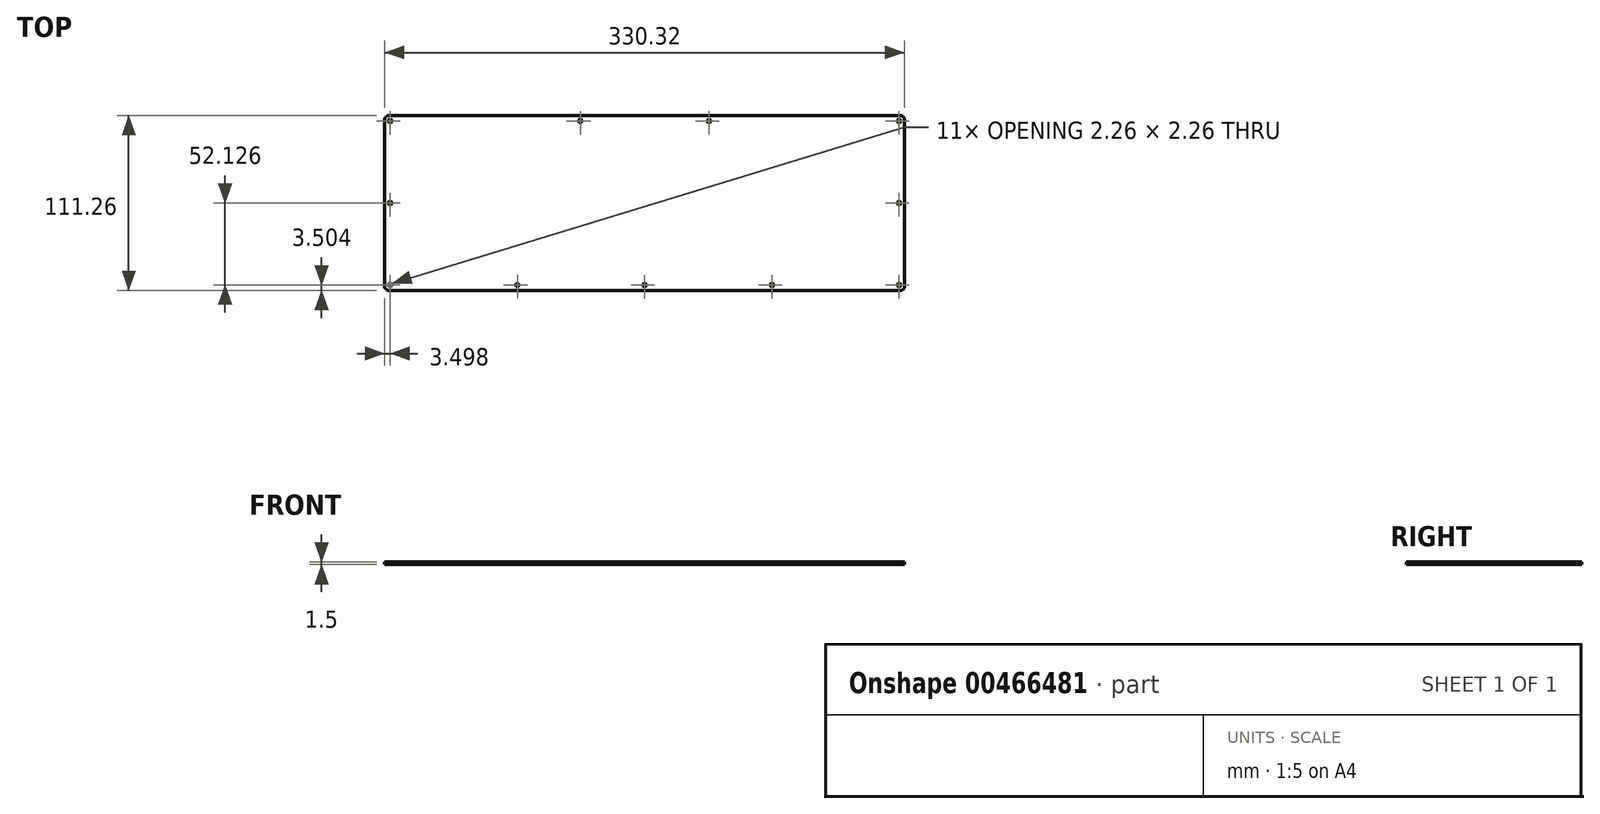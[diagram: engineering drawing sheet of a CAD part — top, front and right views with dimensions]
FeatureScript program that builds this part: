
annotation { "Feature Type Name" : "Feature", "Feature Type Description" : "" }
export const myFeature = defineFeature(function(context is Context, id is Id, definition is map)
    precondition{}
    {
        {
            var Q0;
            Q0=qCreatedBy(makeId("Top.planeOp"),FACE);
            var sketch = newSketch(context, id + "F0", { "sketchPlane" : qUnion([Q0])});
            skLineSegment(sketch, "E0", {"start": v(162.16, 55.62) * mm, "end": v(162.4, 55.62) * mm});
            skLineSegment(sketch, "E1", {"start": v(162.4, 55.62) * mm, "end": v(162.63, 55.59) * mm});
            skLineSegment(sketch, "E2", {"start": v(162.63, 55.59) * mm, "end": v(162.86, 55.54) * mm});
            skLineSegment(sketch, "E3", {"start": v(162.86, 55.54) * mm, "end": v(163.1, 55.48) * mm});
            skLineSegment(sketch, "E4", {"start": v(163.1, 55.48) * mm, "end": v(163.31, 55.4) * mm});
            skLineSegment(sketch, "E5", {"start": v(163.31, 55.4) * mm, "end": v(163.53, 55.3) * mm});
            skLineSegment(sketch, "E6", {"start": v(163.53, 55.3) * mm, "end": v(163.73, 55.18) * mm});
            skLineSegment(sketch, "E7", {"start": v(163.73, 55.18) * mm, "end": v(163.93, 55.05) * mm});
            skLineSegment(sketch, "E8", {"start": v(163.93, 55.05) * mm, "end": v(164.11, 54.9) * mm});
            skLineSegment(sketch, "E9", {"start": v(164.11, 54.9) * mm, "end": v(164.29, 54.75) * mm});
            skLineSegment(sketch, "E10", {"start": v(164.29, 54.75) * mm, "end": v(164.45, 54.57) * mm});
            skLineSegment(sketch, "E11", {"start": v(164.45, 54.57) * mm, "end": v(164.6, 54.39) * mm});
            skLineSegment(sketch, "E12", {"start": v(164.6, 54.39) * mm, "end": v(164.72, 54.2) * mm});
            skLineSegment(sketch, "E13", {"start": v(164.72, 54.2) * mm, "end": v(164.84, 53.99) * mm});
            skLineSegment(sketch, "E14", {"start": v(164.84, 53.99) * mm, "end": v(164.93, 53.77) * mm});
            skLineSegment(sketch, "E15", {"start": v(164.93, 53.77) * mm, "end": v(165.02, 53.55) * mm});
            skLineSegment(sketch, "E16", {"start": v(165.02, 53.55) * mm, "end": v(165.08, 53.33) * mm});
            skLineSegment(sketch, "E17", {"start": v(165.08, 53.33) * mm, "end": v(165.13, 53.1) * mm});
            skLineSegment(sketch, "E18", {"start": v(165.13, 53.1) * mm, "end": v(165.15, 52.86) * mm});
            skLineSegment(sketch, "E19", {"start": v(165.15, 52.86) * mm, "end": v(165.16, 52.62) * mm});
            skLineSegment(sketch, "E20", {"start": v(165.16, 52.62) * mm, "end": v(165.16, -52.63) * mm});
            skLineSegment(sketch, "E21", {"start": v(165.16, -52.63) * mm, "end": v(165.15, -52.86) * mm});
            skLineSegment(sketch, "E22", {"start": v(165.15, -52.86) * mm, "end": v(165.13, -53.1) * mm});
            skLineSegment(sketch, "E23", {"start": v(165.13, -53.1) * mm, "end": v(165.08, -53.33) * mm});
            skLineSegment(sketch, "E24", {"start": v(165.08, -53.33) * mm, "end": v(165.02, -53.55) * mm});
            skLineSegment(sketch, "E25", {"start": v(165.02, -53.55) * mm, "end": v(164.93, -53.77) * mm});
            skLineSegment(sketch, "E26", {"start": v(164.93, -53.77) * mm, "end": v(164.84, -53.99) * mm});
            skLineSegment(sketch, "E27", {"start": v(164.84, -53.99) * mm, "end": v(164.72, -54.2) * mm});
            skLineSegment(sketch, "E28", {"start": v(164.72, -54.2) * mm, "end": v(164.6, -54.39) * mm});
            skLineSegment(sketch, "E29", {"start": v(164.6, -54.39) * mm, "end": v(164.45, -54.57) * mm});
            skLineSegment(sketch, "E30", {"start": v(164.45, -54.57) * mm, "end": v(164.29, -54.75) * mm});
            skLineSegment(sketch, "E31", {"start": v(164.29, -54.75) * mm, "end": v(164.11, -54.9) * mm});
            skLineSegment(sketch, "E32", {"start": v(164.11, -54.9) * mm, "end": v(163.93, -55.05) * mm});
            skLineSegment(sketch, "E33", {"start": v(163.93, -55.05) * mm, "end": v(163.73, -55.18) * mm});
            skLineSegment(sketch, "E34", {"start": v(163.73, -55.18) * mm, "end": v(163.53, -55.3) * mm});
            skLineSegment(sketch, "E35", {"start": v(163.53, -55.3) * mm, "end": v(163.31, -55.4) * mm});
            skLineSegment(sketch, "E36", {"start": v(163.31, -55.4) * mm, "end": v(163.1, -55.48) * mm});
            skLineSegment(sketch, "E37", {"start": v(163.1, -55.48) * mm, "end": v(162.86, -55.54) * mm});
            skLineSegment(sketch, "E38", {"start": v(162.86, -55.54) * mm, "end": v(162.63, -55.59) * mm});
            skLineSegment(sketch, "E39", {"start": v(162.63, -55.59) * mm, "end": v(162.4, -55.62) * mm});
            skLineSegment(sketch, "E40", {"start": v(162.4, -55.62) * mm, "end": v(162.16, -55.63) * mm});
            skLineSegment(sketch, "E41", {"start": v(162.16, -55.63) * mm, "end": v(-162.16, -55.63) * mm});
            skLineSegment(sketch, "E42", {"start": v(-162.16, -55.63) * mm, "end": v(-162.4, -55.62) * mm});
            skLineSegment(sketch, "E43", {"start": v(-162.4, -55.62) * mm, "end": v(-162.63, -55.59) * mm});
            skLineSegment(sketch, "E44", {"start": v(-162.63, -55.59) * mm, "end": v(-162.86, -55.54) * mm});
            skLineSegment(sketch, "E45", {"start": v(-162.86, -55.54) * mm, "end": v(-163.09, -55.48) * mm});
            skLineSegment(sketch, "E46", {"start": v(-163.09, -55.48) * mm, "end": v(-163.31, -55.4) * mm});
            skLineSegment(sketch, "E47", {"start": v(-163.31, -55.4) * mm, "end": v(-163.52, -55.3) * mm});
            skLineSegment(sketch, "E48", {"start": v(-163.52, -55.3) * mm, "end": v(-163.73, -55.18) * mm});
            skLineSegment(sketch, "E49", {"start": v(-163.73, -55.18) * mm, "end": v(-163.93, -55.05) * mm});
            skLineSegment(sketch, "E50", {"start": v(-163.93, -55.05) * mm, "end": v(-164.11, -54.9) * mm});
            skLineSegment(sketch, "E51", {"start": v(-164.11, -54.9) * mm, "end": v(-164.28, -54.75) * mm});
            skLineSegment(sketch, "E52", {"start": v(-164.28, -54.75) * mm, "end": v(-164.44, -54.57) * mm});
            skLineSegment(sketch, "E53", {"start": v(-164.44, -54.57) * mm, "end": v(-164.6, -54.39) * mm});
            skLineSegment(sketch, "E54", {"start": v(-164.6, -54.39) * mm, "end": v(-164.72, -54.2) * mm});
            skLineSegment(sketch, "E55", {"start": v(-164.72, -54.2) * mm, "end": v(-164.84, -53.99) * mm});
            skLineSegment(sketch, "E56", {"start": v(-164.84, -53.99) * mm, "end": v(-164.93, -53.77) * mm});
            skLineSegment(sketch, "E57", {"start": v(-164.93, -53.77) * mm, "end": v(-165.02, -53.55) * mm});
            skLineSegment(sketch, "E58", {"start": v(-165.02, -53.55) * mm, "end": v(-165.08, -53.33) * mm});
            skLineSegment(sketch, "E59", {"start": v(-165.08, -53.33) * mm, "end": v(-165.13, -53.1) * mm});
            skLineSegment(sketch, "E60", {"start": v(-165.13, -53.1) * mm, "end": v(-165.15, -52.86) * mm});
            skLineSegment(sketch, "E61", {"start": v(-165.15, -52.86) * mm, "end": v(-165.16, -52.63) * mm});
            skLineSegment(sketch, "E62", {"start": v(-165.16, -52.63) * mm, "end": v(-165.16, 52.62) * mm});
            skLineSegment(sketch, "E63", {"start": v(-165.16, 52.62) * mm, "end": v(-165.15, 52.86) * mm});
            skLineSegment(sketch, "E64", {"start": v(-165.15, 52.86) * mm, "end": v(-165.13, 53.1) * mm});
            skLineSegment(sketch, "E65", {"start": v(-165.13, 53.1) * mm, "end": v(-165.08, 53.33) * mm});
            skLineSegment(sketch, "E66", {"start": v(-165.08, 53.33) * mm, "end": v(-165.02, 53.55) * mm});
            skLineSegment(sketch, "E67", {"start": v(-165.02, 53.55) * mm, "end": v(-164.93, 53.77) * mm});
            skLineSegment(sketch, "E68", {"start": v(-164.93, 53.77) * mm, "end": v(-164.84, 53.99) * mm});
            skLineSegment(sketch, "E69", {"start": v(-164.84, 53.99) * mm, "end": v(-164.72, 54.2) * mm});
            skLineSegment(sketch, "E70", {"start": v(-164.72, 54.2) * mm, "end": v(-164.6, 54.39) * mm});
            skLineSegment(sketch, "E71", {"start": v(-164.6, 54.39) * mm, "end": v(-164.44, 54.57) * mm});
            skLineSegment(sketch, "E72", {"start": v(-164.44, 54.57) * mm, "end": v(-164.28, 54.75) * mm});
            skLineSegment(sketch, "E73", {"start": v(-164.28, 54.75) * mm, "end": v(-164.11, 54.9) * mm});
            skLineSegment(sketch, "E74", {"start": v(-164.11, 54.9) * mm, "end": v(-163.93, 55.05) * mm});
            skLineSegment(sketch, "E75", {"start": v(-163.93, 55.05) * mm, "end": v(-163.73, 55.18) * mm});
            skLineSegment(sketch, "E76", {"start": v(-163.73, 55.18) * mm, "end": v(-163.52, 55.3) * mm});
            skLineSegment(sketch, "E77", {"start": v(-163.52, 55.3) * mm, "end": v(-163.31, 55.4) * mm});
            skLineSegment(sketch, "E78", {"start": v(-163.31, 55.4) * mm, "end": v(-163.09, 55.48) * mm});
            skLineSegment(sketch, "E79", {"start": v(-163.09, 55.48) * mm, "end": v(-162.86, 55.54) * mm});
            skLineSegment(sketch, "E80", {"start": v(-162.86, 55.54) * mm, "end": v(-162.63, 55.59) * mm});
            skLineSegment(sketch, "E81", {"start": v(-162.63, 55.59) * mm, "end": v(-162.4, 55.62) * mm});
            skLineSegment(sketch, "E82", {"start": v(-162.4, 55.62) * mm, "end": v(-162.16, 55.63) * mm});
            skLineSegment(sketch, "E83", {"start": v(-162.16, 55.63) * mm, "end": v(162.16, 55.62) * mm});
            skLineSegment(sketch, "E84", {"start": v(161.31, -51.05) * mm, "end": v(161, -51.21) * mm});
            skLineSegment(sketch, "E85", {"start": v(161, -51.21) * mm, "end": v(160.75, -51.46) * mm});
            skLineSegment(sketch, "E86", {"start": v(160.75, -51.46) * mm, "end": v(160.59, -51.78) * mm});
            skLineSegment(sketch, "E87", {"start": v(160.59, -51.78) * mm, "end": v(160.53, -52.13) * mm});
            skLineSegment(sketch, "E88", {"start": v(160.53, -52.13) * mm, "end": v(160.59, -52.48) * mm});
            skLineSegment(sketch, "E89", {"start": v(160.59, -52.48) * mm, "end": v(160.75, -52.79) * mm});
            skLineSegment(sketch, "E90", {"start": v(160.75, -52.79) * mm, "end": v(161, -53.04) * mm});
            skLineSegment(sketch, "E91", {"start": v(161, -53.04) * mm, "end": v(161.31, -53.2) * mm});
            skLineSegment(sketch, "E92", {"start": v(161.31, -53.2) * mm, "end": v(161.66, -53.26) * mm});
            skLineSegment(sketch, "E93", {"start": v(161.66, -53.26) * mm, "end": v(162.01, -53.2) * mm});
            skLineSegment(sketch, "E94", {"start": v(162.01, -53.2) * mm, "end": v(162.33, -53.04) * mm});
            skLineSegment(sketch, "E95", {"start": v(162.33, -53.04) * mm, "end": v(162.58, -52.79) * mm});
            skLineSegment(sketch, "E96", {"start": v(162.58, -52.79) * mm, "end": v(162.74, -52.48) * mm});
            skLineSegment(sketch, "E97", {"start": v(162.74, -52.48) * mm, "end": v(162.8, -52.13) * mm});
            skLineSegment(sketch, "E98", {"start": v(162.8, -52.13) * mm, "end": v(162.74, -51.78) * mm});
            skLineSegment(sketch, "E99", {"start": v(162.74, -51.78) * mm, "end": v(162.58, -51.46) * mm});
            skLineSegment(sketch, "E100", {"start": v(162.58, -51.46) * mm, "end": v(162.33, -51.21) * mm});
            skLineSegment(sketch, "E101", {"start": v(162.33, -51.21) * mm, "end": v(162.01, -51.05) * mm});
            skLineSegment(sketch, "E102", {"start": v(162.01, -51.05) * mm, "end": v(161.66, -51) * mm});
            skLineSegment(sketch, "E103", {"start": v(161.66, -51) * mm, "end": v(161.31, -51.05) * mm});
            skLineSegment(sketch, "E104", {"start": v(80.48, -51.05) * mm, "end": v(80.17, -51.21) * mm});
            skLineSegment(sketch, "E105", {"start": v(80.17, -51.21) * mm, "end": v(79.92, -51.46) * mm});
            skLineSegment(sketch, "E106", {"start": v(79.92, -51.46) * mm, "end": v(79.76, -51.78) * mm});
            skLineSegment(sketch, "E107", {"start": v(79.76, -51.78) * mm, "end": v(79.7, -52.13) * mm});
            skLineSegment(sketch, "E108", {"start": v(79.7, -52.13) * mm, "end": v(79.76, -52.48) * mm});
            skLineSegment(sketch, "E109", {"start": v(79.76, -52.48) * mm, "end": v(79.92, -52.79) * mm});
            skLineSegment(sketch, "E110", {"start": v(79.92, -52.79) * mm, "end": v(80.17, -53.04) * mm});
            skLineSegment(sketch, "E111", {"start": v(80.17, -53.04) * mm, "end": v(80.48, -53.2) * mm});
            skLineSegment(sketch, "E112", {"start": v(80.48, -53.2) * mm, "end": v(80.83, -53.26) * mm});
            skLineSegment(sketch, "E113", {"start": v(80.83, -53.26) * mm, "end": v(81.18, -53.2) * mm});
            skLineSegment(sketch, "E114", {"start": v(81.18, -53.2) * mm, "end": v(81.5, -53.04) * mm});
            skLineSegment(sketch, "E115", {"start": v(81.5, -53.04) * mm, "end": v(81.75, -52.79) * mm});
            skLineSegment(sketch, "E116", {"start": v(81.75, -52.79) * mm, "end": v(81.9, -52.48) * mm});
            skLineSegment(sketch, "E117", {"start": v(81.9, -52.48) * mm, "end": v(81.96, -52.13) * mm});
            skLineSegment(sketch, "E118", {"start": v(81.96, -52.13) * mm, "end": v(81.9, -51.78) * mm});
            skLineSegment(sketch, "E119", {"start": v(81.9, -51.78) * mm, "end": v(81.75, -51.46) * mm});
            skLineSegment(sketch, "E120", {"start": v(81.75, -51.46) * mm, "end": v(81.5, -51.21) * mm});
            skLineSegment(sketch, "E121", {"start": v(81.5, -51.21) * mm, "end": v(81.18, -51.05) * mm});
            skLineSegment(sketch, "E122", {"start": v(81.18, -51.05) * mm, "end": v(80.83, -51) * mm});
            skLineSegment(sketch, "E123", {"start": v(80.83, -51) * mm, "end": v(80.48, -51.05) * mm});
            skLineSegment(sketch, "E124", {"start": v(-0.35, -51.05) * mm, "end": v(-0.66, -51.21) * mm});
            skLineSegment(sketch, "E125", {"start": v(-0.66, -51.21) * mm, "end": v(-0.91, -51.46) * mm});
            skLineSegment(sketch, "E126", {"start": v(-0.91, -51.46) * mm, "end": v(-1.07, -51.78) * mm});
            skLineSegment(sketch, "E127", {"start": v(-1.07, -51.78) * mm, "end": v(-1.13, -52.13) * mm});
            skLineSegment(sketch, "E128", {"start": v(-1.13, -52.13) * mm, "end": v(-1.07, -52.48) * mm});
            skLineSegment(sketch, "E129", {"start": v(-1.07, -52.48) * mm, "end": v(-0.91, -52.79) * mm});
            skLineSegment(sketch, "E130", {"start": v(-0.91, -52.79) * mm, "end": v(-0.66, -53.04) * mm});
            skLineSegment(sketch, "E131", {"start": v(-0.66, -53.04) * mm, "end": v(-0.35, -53.2) * mm});
            skLineSegment(sketch, "E132", {"start": v(-0.35, -53.2) * mm, "end": v(0, -53.26) * mm});
            skLineSegment(sketch, "E133", {"start": v(0, -53.26) * mm, "end": v(0.35, -53.2) * mm});
            skLineSegment(sketch, "E134", {"start": v(0.35, -53.2) * mm, "end": v(0.67, -53.04) * mm});
            skLineSegment(sketch, "E135", {"start": v(0.67, -53.04) * mm, "end": v(0.92, -52.79) * mm});
            skLineSegment(sketch, "E136", {"start": v(0.92, -52.79) * mm, "end": v(1.07, -52.48) * mm});
            skLineSegment(sketch, "E137", {"start": v(1.07, -52.48) * mm, "end": v(1.13, -52.13) * mm});
            skLineSegment(sketch, "E138", {"start": v(1.13, -52.13) * mm, "end": v(1.07, -51.78) * mm});
            skLineSegment(sketch, "E139", {"start": v(1.07, -51.78) * mm, "end": v(0.92, -51.46) * mm});
            skLineSegment(sketch, "E140", {"start": v(0.92, -51.46) * mm, "end": v(0.67, -51.21) * mm});
            skLineSegment(sketch, "E141", {"start": v(0.67, -51.21) * mm, "end": v(0.35, -51.05) * mm});
            skLineSegment(sketch, "E142", {"start": v(0.35, -51.05) * mm, "end": v(0, -51) * mm});
            skLineSegment(sketch, "E143", {"start": v(0, -51) * mm, "end": v(-0.35, -51.05) * mm});
            skLineSegment(sketch, "E144", {"start": v(-81.18, -51.05) * mm, "end": v(-81.5, -51.21) * mm});
            skLineSegment(sketch, "E145", {"start": v(-81.5, -51.21) * mm, "end": v(-81.75, -51.46) * mm});
            skLineSegment(sketch, "E146", {"start": v(-81.75, -51.46) * mm, "end": v(-81.9, -51.78) * mm});
            skLineSegment(sketch, "E147", {"start": v(-81.9, -51.78) * mm, "end": v(-81.96, -52.13) * mm});
            skLineSegment(sketch, "E148", {"start": v(-81.96, -52.13) * mm, "end": v(-81.9, -52.48) * mm});
            skLineSegment(sketch, "E149", {"start": v(-81.9, -52.48) * mm, "end": v(-81.75, -52.79) * mm});
            skLineSegment(sketch, "E150", {"start": v(-81.75, -52.79) * mm, "end": v(-81.5, -53.04) * mm});
            skLineSegment(sketch, "E151", {"start": v(-81.5, -53.04) * mm, "end": v(-81.18, -53.2) * mm});
            skLineSegment(sketch, "E152", {"start": v(-81.18, -53.2) * mm, "end": v(-80.83, -53.26) * mm});
            skLineSegment(sketch, "E153", {"start": v(-80.83, -53.26) * mm, "end": v(-80.48, -53.2) * mm});
            skLineSegment(sketch, "E154", {"start": v(-80.48, -53.2) * mm, "end": v(-80.17, -53.04) * mm});
            skLineSegment(sketch, "E155", {"start": v(-80.17, -53.04) * mm, "end": v(-79.92, -52.79) * mm});
            skLineSegment(sketch, "E156", {"start": v(-79.92, -52.79) * mm, "end": v(-79.76, -52.48) * mm});
            skLineSegment(sketch, "E157", {"start": v(-79.76, -52.48) * mm, "end": v(-79.7, -52.13) * mm});
            skLineSegment(sketch, "E158", {"start": v(-79.7, -52.13) * mm, "end": v(-79.76, -51.78) * mm});
            skLineSegment(sketch, "E159", {"start": v(-79.76, -51.78) * mm, "end": v(-79.92, -51.46) * mm});
            skLineSegment(sketch, "E160", {"start": v(-79.92, -51.46) * mm, "end": v(-80.17, -51.21) * mm});
            skLineSegment(sketch, "E161", {"start": v(-80.17, -51.21) * mm, "end": v(-80.48, -51.05) * mm});
            skLineSegment(sketch, "E162", {"start": v(-80.48, -51.05) * mm, "end": v(-80.83, -51) * mm});
            skLineSegment(sketch, "E163", {"start": v(-80.83, -51) * mm, "end": v(-81.18, -51.05) * mm});
            skLineSegment(sketch, "E164", {"start": v(-162.01, -51.05) * mm, "end": v(-162.33, -51.21) * mm});
            skLineSegment(sketch, "E165", {"start": v(-162.33, -51.21) * mm, "end": v(-162.58, -51.46) * mm});
            skLineSegment(sketch, "E166", {"start": v(-162.58, -51.46) * mm, "end": v(-162.74, -51.78) * mm});
            skLineSegment(sketch, "E167", {"start": v(-162.74, -51.78) * mm, "end": v(-162.8, -52.13) * mm});
            skLineSegment(sketch, "E168", {"start": v(-162.8, -52.13) * mm, "end": v(-162.74, -52.48) * mm});
            skLineSegment(sketch, "E169", {"start": v(-162.74, -52.48) * mm, "end": v(-162.58, -52.79) * mm});
            skLineSegment(sketch, "E170", {"start": v(-162.58, -52.79) * mm, "end": v(-162.33, -53.04) * mm});
            skLineSegment(sketch, "E171", {"start": v(-162.33, -53.04) * mm, "end": v(-162.01, -53.2) * mm});
            skLineSegment(sketch, "E172", {"start": v(-162.01, -53.2) * mm, "end": v(-161.66, -53.26) * mm});
            skLineSegment(sketch, "E173", {"start": v(-161.66, -53.26) * mm, "end": v(-161.31, -53.2) * mm});
            skLineSegment(sketch, "E174", {"start": v(-161.31, -53.2) * mm, "end": v(-161, -53.04) * mm});
            skLineSegment(sketch, "E175", {"start": v(-161, -53.04) * mm, "end": v(-160.75, -52.79) * mm});
            skLineSegment(sketch, "E176", {"start": v(-160.75, -52.79) * mm, "end": v(-160.59, -52.48) * mm});
            skLineSegment(sketch, "E177", {"start": v(-160.59, -52.48) * mm, "end": v(-160.53, -52.13) * mm});
            skLineSegment(sketch, "E178", {"start": v(-160.53, -52.13) * mm, "end": v(-160.59, -51.78) * mm});
            skLineSegment(sketch, "E179", {"start": v(-160.59, -51.78) * mm, "end": v(-160.75, -51.46) * mm});
            skLineSegment(sketch, "E180", {"start": v(-160.75, -51.46) * mm, "end": v(-161, -51.21) * mm});
            skLineSegment(sketch, "E181", {"start": v(-161, -51.21) * mm, "end": v(-161.31, -51.05) * mm});
            skLineSegment(sketch, "E182", {"start": v(-161.31, -51.05) * mm, "end": v(-161.66, -51) * mm});
            skLineSegment(sketch, "E183", {"start": v(-161.66, -51) * mm, "end": v(-162.01, -51.05) * mm});
            skLineSegment(sketch, "E184", {"start": v(161.31, 1.08) * mm, "end": v(161, 0.91) * mm});
            skLineSegment(sketch, "E185", {"start": v(161, 0.91) * mm, "end": v(160.75, 0.66) * mm});
            skLineSegment(sketch, "E186", {"start": v(160.75, 0.66) * mm, "end": v(160.59, 0.35) * mm});
            skLineSegment(sketch, "E187", {"start": v(160.59, 0.35) * mm, "end": v(160.53, 0) * mm});
            skLineSegment(sketch, "E188", {"start": v(160.53, 0) * mm, "end": v(160.59, -0.35) * mm});
            skLineSegment(sketch, "E189", {"start": v(160.59, -0.35) * mm, "end": v(160.75, -0.66) * mm});
            skLineSegment(sketch, "E190", {"start": v(160.75, -0.66) * mm, "end": v(161, -0.91) * mm});
            skLineSegment(sketch, "E191", {"start": v(161, -0.91) * mm, "end": v(161.31, -1.07) * mm});
            skLineSegment(sketch, "E192", {"start": v(161.31, -1.07) * mm, "end": v(161.66, -1.13) * mm});
            skLineSegment(sketch, "E193", {"start": v(161.66, -1.13) * mm, "end": v(162.01, -1.07) * mm});
            skLineSegment(sketch, "E194", {"start": v(162.01, -1.07) * mm, "end": v(162.33, -0.91) * mm});
            skLineSegment(sketch, "E195", {"start": v(162.33, -0.91) * mm, "end": v(162.58, -0.66) * mm});
            skLineSegment(sketch, "E196", {"start": v(162.58, -0.66) * mm, "end": v(162.74, -0.35) * mm});
            skLineSegment(sketch, "E197", {"start": v(162.74, -0.35) * mm, "end": v(162.8, 0) * mm});
            skLineSegment(sketch, "E198", {"start": v(162.8, 0) * mm, "end": v(162.74, 0.35) * mm});
            skLineSegment(sketch, "E199", {"start": v(162.74, 0.35) * mm, "end": v(162.58, 0.66) * mm});
            skLineSegment(sketch, "E200", {"start": v(162.58, 0.66) * mm, "end": v(162.33, 0.91) * mm});
            skLineSegment(sketch, "E201", {"start": v(162.33, 0.91) * mm, "end": v(162.01, 1.08) * mm});
            skLineSegment(sketch, "E202", {"start": v(162.01, 1.08) * mm, "end": v(161.66, 1.13) * mm});
            skLineSegment(sketch, "E203", {"start": v(161.66, 1.13) * mm, "end": v(161.31, 1.08) * mm});
            skLineSegment(sketch, "E204", {"start": v(-162.01, 1.08) * mm, "end": v(-162.33, 0.91) * mm});
            skLineSegment(sketch, "E205", {"start": v(-162.33, 0.91) * mm, "end": v(-162.58, 0.66) * mm});
            skLineSegment(sketch, "E206", {"start": v(-162.58, 0.66) * mm, "end": v(-162.74, 0.35) * mm});
            skLineSegment(sketch, "E207", {"start": v(-162.74, 0.35) * mm, "end": v(-162.8, 0) * mm});
            skLineSegment(sketch, "E208", {"start": v(-162.8, 0) * mm, "end": v(-162.74, -0.35) * mm});
            skLineSegment(sketch, "E209", {"start": v(-162.74, -0.35) * mm, "end": v(-162.58, -0.66) * mm});
            skLineSegment(sketch, "E210", {"start": v(-162.58, -0.66) * mm, "end": v(-162.33, -0.91) * mm});
            skLineSegment(sketch, "E211", {"start": v(-162.33, -0.91) * mm, "end": v(-162.01, -1.07) * mm});
            skLineSegment(sketch, "E212", {"start": v(-162.01, -1.07) * mm, "end": v(-161.66, -1.13) * mm});
            skLineSegment(sketch, "E213", {"start": v(-161.66, -1.13) * mm, "end": v(-161.31, -1.07) * mm});
            skLineSegment(sketch, "E214", {"start": v(-161.31, -1.07) * mm, "end": v(-161, -0.91) * mm});
            skLineSegment(sketch, "E215", {"start": v(-161, -0.91) * mm, "end": v(-160.75, -0.66) * mm});
            skLineSegment(sketch, "E216", {"start": v(-160.75, -0.66) * mm, "end": v(-160.59, -0.35) * mm});
            skLineSegment(sketch, "E217", {"start": v(-160.59, -0.35) * mm, "end": v(-160.53, 0) * mm});
            skLineSegment(sketch, "E218", {"start": v(-160.53, 0) * mm, "end": v(-160.59, 0.35) * mm});
            skLineSegment(sketch, "E219", {"start": v(-160.59, 0.35) * mm, "end": v(-160.75, 0.66) * mm});
            skLineSegment(sketch, "E220", {"start": v(-160.75, 0.66) * mm, "end": v(-161, 0.91) * mm});
            skLineSegment(sketch, "E221", {"start": v(-161, 0.91) * mm, "end": v(-161.31, 1.08) * mm});
            skLineSegment(sketch, "E222", {"start": v(-161.31, 1.08) * mm, "end": v(-161.66, 1.13) * mm});
            skLineSegment(sketch, "E223", {"start": v(-161.66, 1.13) * mm, "end": v(-162.01, 1.08) * mm});
            skLineSegment(sketch, "E224", {"start": v(-41.18, 53.2) * mm, "end": v(-41.5, 53.04) * mm});
            skLineSegment(sketch, "E225", {"start": v(-41.5, 53.04) * mm, "end": v(-41.75, 52.8) * mm});
            skLineSegment(sketch, "E226", {"start": v(-41.75, 52.8) * mm, "end": v(-41.9, 52.47) * mm});
            skLineSegment(sketch, "E227", {"start": v(-41.9, 52.47) * mm, "end": v(-41.96, 52.12) * mm});
            skLineSegment(sketch, "E228", {"start": v(-41.96, 52.12) * mm, "end": v(-41.9, 51.78) * mm});
            skLineSegment(sketch, "E229", {"start": v(-41.9, 51.78) * mm, "end": v(-41.75, 51.46) * mm});
            skLineSegment(sketch, "E230", {"start": v(-41.75, 51.46) * mm, "end": v(-41.5, 51.21) * mm});
            skLineSegment(sketch, "E231", {"start": v(-41.5, 51.21) * mm, "end": v(-41.18, 51.05) * mm});
            skLineSegment(sketch, "E232", {"start": v(-41.18, 51.05) * mm, "end": v(-40.83, 51) * mm});
            skLineSegment(sketch, "E233", {"start": v(-40.83, 51) * mm, "end": v(-40.48, 51.05) * mm});
            skLineSegment(sketch, "E234", {"start": v(-40.48, 51.05) * mm, "end": v(-40.17, 51.21) * mm});
            skLineSegment(sketch, "E235", {"start": v(-40.17, 51.21) * mm, "end": v(-39.92, 51.46) * mm});
            skLineSegment(sketch, "E236", {"start": v(-39.92, 51.46) * mm, "end": v(-39.76, 51.78) * mm});
            skLineSegment(sketch, "E237", {"start": v(-39.76, 51.78) * mm, "end": v(-39.7, 52.12) * mm});
            skLineSegment(sketch, "E238", {"start": v(-39.7, 52.12) * mm, "end": v(-39.76, 52.47) * mm});
            skLineSegment(sketch, "E239", {"start": v(-39.76, 52.47) * mm, "end": v(-39.92, 52.8) * mm});
            skLineSegment(sketch, "E240", {"start": v(-39.92, 52.8) * mm, "end": v(-40.17, 53.04) * mm});
            skLineSegment(sketch, "E241", {"start": v(-40.17, 53.04) * mm, "end": v(-40.48, 53.2) * mm});
            skLineSegment(sketch, "E242", {"start": v(-40.48, 53.2) * mm, "end": v(-40.83, 53.26) * mm});
            skLineSegment(sketch, "E243", {"start": v(-40.83, 53.26) * mm, "end": v(-41.18, 53.2) * mm});
            skLineSegment(sketch, "E244", {"start": v(40.48, 53.2) * mm, "end": v(40.17, 53.04) * mm});
            skLineSegment(sketch, "E245", {"start": v(40.17, 53.04) * mm, "end": v(39.92, 52.8) * mm});
            skLineSegment(sketch, "E246", {"start": v(39.92, 52.8) * mm, "end": v(39.76, 52.47) * mm});
            skLineSegment(sketch, "E247", {"start": v(39.76, 52.47) * mm, "end": v(39.7, 52.12) * mm});
            skLineSegment(sketch, "E248", {"start": v(39.7, 52.12) * mm, "end": v(39.76, 51.78) * mm});
            skLineSegment(sketch, "E249", {"start": v(39.76, 51.78) * mm, "end": v(39.92, 51.46) * mm});
            skLineSegment(sketch, "E250", {"start": v(39.92, 51.46) * mm, "end": v(40.17, 51.21) * mm});
            skLineSegment(sketch, "E251", {"start": v(40.17, 51.21) * mm, "end": v(40.48, 51.05) * mm});
            skLineSegment(sketch, "E252", {"start": v(40.48, 51.05) * mm, "end": v(40.83, 51) * mm});
            skLineSegment(sketch, "E253", {"start": v(40.83, 51) * mm, "end": v(41.18, 51.05) * mm});
            skLineSegment(sketch, "E254", {"start": v(41.18, 51.05) * mm, "end": v(41.5, 51.21) * mm});
            skLineSegment(sketch, "E255", {"start": v(41.5, 51.21) * mm, "end": v(41.75, 51.46) * mm});
            skLineSegment(sketch, "E256", {"start": v(41.75, 51.46) * mm, "end": v(41.9, 51.78) * mm});
            skLineSegment(sketch, "E257", {"start": v(41.9, 51.78) * mm, "end": v(41.96, 52.12) * mm});
            skLineSegment(sketch, "E258", {"start": v(41.96, 52.12) * mm, "end": v(41.9, 52.47) * mm});
            skLineSegment(sketch, "E259", {"start": v(41.9, 52.47) * mm, "end": v(41.75, 52.8) * mm});
            skLineSegment(sketch, "E260", {"start": v(41.75, 52.8) * mm, "end": v(41.5, 53.04) * mm});
            skLineSegment(sketch, "E261", {"start": v(41.5, 53.04) * mm, "end": v(41.18, 53.2) * mm});
            skLineSegment(sketch, "E262", {"start": v(41.18, 53.2) * mm, "end": v(40.83, 53.26) * mm});
            skLineSegment(sketch, "E263", {"start": v(40.83, 53.26) * mm, "end": v(40.48, 53.2) * mm});
            skLineSegment(sketch, "E264", {"start": v(161.31, 53.2) * mm, "end": v(161, 53.04) * mm});
            skLineSegment(sketch, "E265", {"start": v(161, 53.04) * mm, "end": v(160.75, 52.8) * mm});
            skLineSegment(sketch, "E266", {"start": v(160.75, 52.8) * mm, "end": v(160.59, 52.47) * mm});
            skLineSegment(sketch, "E267", {"start": v(160.59, 52.47) * mm, "end": v(160.53, 52.12) * mm});
            skLineSegment(sketch, "E268", {"start": v(160.53, 52.12) * mm, "end": v(160.59, 51.78) * mm});
            skLineSegment(sketch, "E269", {"start": v(160.59, 51.78) * mm, "end": v(160.75, 51.46) * mm});
            skLineSegment(sketch, "E270", {"start": v(160.75, 51.46) * mm, "end": v(161, 51.21) * mm});
            skLineSegment(sketch, "E271", {"start": v(161, 51.21) * mm, "end": v(161.31, 51.05) * mm});
            skLineSegment(sketch, "E272", {"start": v(161.31, 51.05) * mm, "end": v(161.66, 51) * mm});
            skLineSegment(sketch, "E273", {"start": v(161.66, 51) * mm, "end": v(162.01, 51.05) * mm});
            skLineSegment(sketch, "E274", {"start": v(162.01, 51.05) * mm, "end": v(162.33, 51.21) * mm});
            skLineSegment(sketch, "E275", {"start": v(162.33, 51.21) * mm, "end": v(162.58, 51.46) * mm});
            skLineSegment(sketch, "E276", {"start": v(162.58, 51.46) * mm, "end": v(162.74, 51.78) * mm});
            skLineSegment(sketch, "E277", {"start": v(162.74, 51.78) * mm, "end": v(162.8, 52.12) * mm});
            skLineSegment(sketch, "E278", {"start": v(162.8, 52.12) * mm, "end": v(162.74, 52.47) * mm});
            skLineSegment(sketch, "E279", {"start": v(162.74, 52.47) * mm, "end": v(162.58, 52.8) * mm});
            skLineSegment(sketch, "E280", {"start": v(162.58, 52.8) * mm, "end": v(162.33, 53.04) * mm});
            skLineSegment(sketch, "E281", {"start": v(162.33, 53.04) * mm, "end": v(162.01, 53.2) * mm});
            skLineSegment(sketch, "E282", {"start": v(162.01, 53.2) * mm, "end": v(161.66, 53.26) * mm});
            skLineSegment(sketch, "E283", {"start": v(161.66, 53.26) * mm, "end": v(161.31, 53.2) * mm});
            skLineSegment(sketch, "E284", {"start": v(-162.01, 53.2) * mm, "end": v(-162.33, 53.04) * mm});
            skLineSegment(sketch, "E285", {"start": v(-162.33, 53.04) * mm, "end": v(-162.58, 52.8) * mm});
            skLineSegment(sketch, "E286", {"start": v(-162.58, 52.8) * mm, "end": v(-162.74, 52.47) * mm});
            skLineSegment(sketch, "E287", {"start": v(-162.74, 52.47) * mm, "end": v(-162.8, 52.12) * mm});
            skLineSegment(sketch, "E288", {"start": v(-162.8, 52.12) * mm, "end": v(-162.74, 51.78) * mm});
            skLineSegment(sketch, "E289", {"start": v(-162.74, 51.78) * mm, "end": v(-162.58, 51.46) * mm});
            skLineSegment(sketch, "E290", {"start": v(-162.58, 51.46) * mm, "end": v(-162.33, 51.21) * mm});
            skLineSegment(sketch, "E291", {"start": v(-162.33, 51.21) * mm, "end": v(-162.01, 51.05) * mm});
            skLineSegment(sketch, "E292", {"start": v(-162.01, 51.05) * mm, "end": v(-161.66, 51) * mm});
            skLineSegment(sketch, "E293", {"start": v(-161.66, 51) * mm, "end": v(-161.31, 51.05) * mm});
            skLineSegment(sketch, "E294", {"start": v(-161.31, 51.05) * mm, "end": v(-161, 51.21) * mm});
            skLineSegment(sketch, "E295", {"start": v(-161, 51.21) * mm, "end": v(-160.75, 51.46) * mm});
            skLineSegment(sketch, "E296", {"start": v(-160.75, 51.46) * mm, "end": v(-160.59, 51.78) * mm});
            skLineSegment(sketch, "E297", {"start": v(-160.59, 51.78) * mm, "end": v(-160.53, 52.12) * mm});
            skLineSegment(sketch, "E298", {"start": v(-160.53, 52.12) * mm, "end": v(-160.59, 52.47) * mm});
            skLineSegment(sketch, "E299", {"start": v(-160.59, 52.47) * mm, "end": v(-160.75, 52.8) * mm});
            skLineSegment(sketch, "E300", {"start": v(-160.75, 52.8) * mm, "end": v(-161, 53.04) * mm});
            skLineSegment(sketch, "E301", {"start": v(-161, 53.04) * mm, "end": v(-161.31, 53.2) * mm});
            skLineSegment(sketch, "E302", {"start": v(-161.31, 53.2) * mm, "end": v(-161.66, 53.26) * mm});
            skLineSegment(sketch, "E303", {"start": v(-161.66, 53.26) * mm, "end": v(-162.01, 53.2) * mm});
            skSolve(sketch);
        }
        {
            var Q0;
            Q0=qSketchRegion(id+"F0",true);
            extrude(context, id + "F1", {"entities" : qUnion([Q0]), "depth" : 1.5 * mm});
        }
    });
